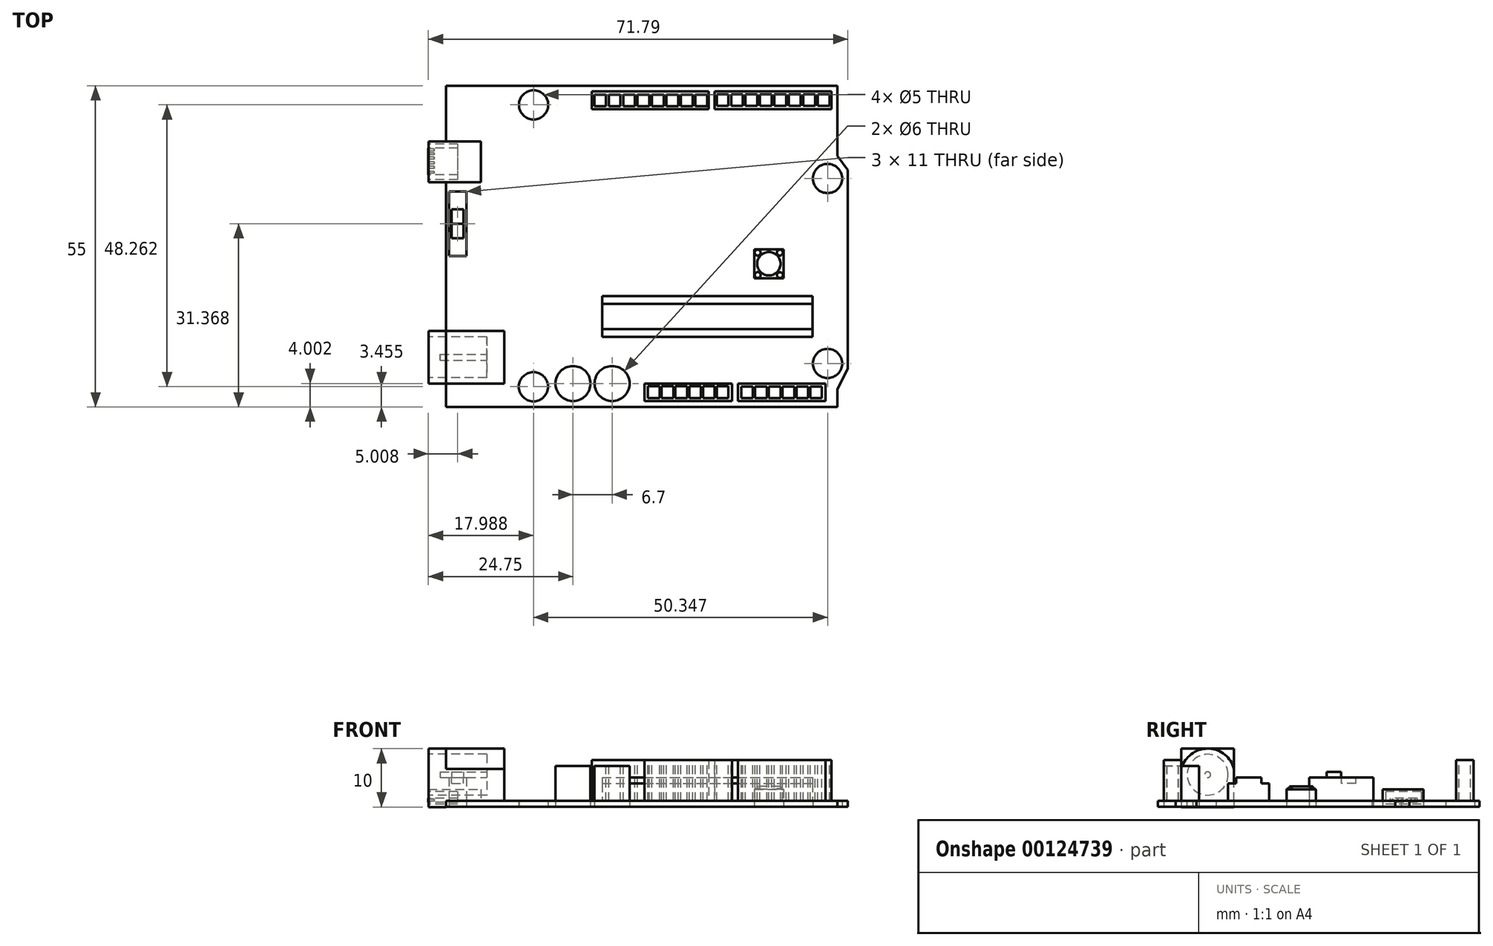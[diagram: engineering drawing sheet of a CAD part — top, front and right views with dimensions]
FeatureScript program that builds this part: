
annotation { "Feature Type Name" : "Feature", "Feature Type Description" : "" }
export const myFeature = defineFeature(function(context is Context, id is Id, definition is map)
    precondition{}
    {
        {
            var Q0;
            Q0=qCreatedBy(makeId("Top.planeOp"),FACE);
            var sketch = newSketch(context, id + "F0", { "sketchPlane" : qUnion([Q0])});
            skLineSegment(sketch, "E0.bottom", {"start": v(-37.2, 39.45) * mm, "end": v(29.8, 39.45) * mm});
            skLineSegment(sketch, "E0.top", {"start": v(-37.2, -15.55) * mm, "end": v(29.8, -15.55) * mm});
            skLineSegment(sketch, "E0.left", {"start": v(-37.2, 39.45) * mm, "end": v(-37.2, -15.55) * mm});
            skLineSegment(sketch, "E0.right", {"start": v(29.8, 39.45) * mm, "end": v(29.8, -15.55) * mm});
            skLineSegment(sketch, "E1", {"start": v(29.8, -12.55) * mm, "end": v(31.59, -8.97) * mm});
            skLineSegment(sketch, "E2", {"start": v(31.59, -8.97) * mm, "end": v(31.59, 25.03) * mm});
            skLineSegment(sketch, "E3", {"start": v(31.59, 25.03) * mm, "end": v(29.8, 27.45) * mm});
            skCircle(sketch, "E4", {"center": v(28.14, -8.11) * mm, "radius": 2.5 * mm});
            skCircle(sketch, "E5", {"center": v(-22.2, 36.17) * mm, "radius": 2.5 * mm});
            skCircle(sketch, "E6", {"center": v(28.14, 23.56) * mm, "radius": 2.5 * mm});
            skLineSegment(sketch, "E7", {"start": v(-22.2, 36.17) * mm, "end": v(-22.2, -14.2) * mm, "construction": true});
            skLineSegment(sketch, "E8", {"start": v(28.14, 23.56) * mm, "end": v(28.14, -13.38) * mm, "construction": true});
            skLineSegment(sketch, "E9.bottom", {"start": v(-40.2, 29.9) * mm, "end": v(-31.2, 29.9) * mm});
            skLineSegment(sketch, "E9.top", {"start": v(-40.2, 22.9) * mm, "end": v(-31.2, 22.9) * mm});
            skLineSegment(sketch, "E9.left", {"start": v(-40.2, 29.9) * mm, "end": v(-40.2, 22.9) * mm});
            skLineSegment(sketch, "E9.right", {"start": v(-31.2, 29.9) * mm, "end": v(-31.2, 22.9) * mm});
            skCircle(sketch, "E10", {"center": v(-22.21, -12.1) * mm, "radius": 2.5 * mm});
            skLineSegment(sketch, "E11.bottom", {"start": v(-3.2, -11.55) * mm, "end": v(11.8, -11.55) * mm});
            skLineSegment(sketch, "E11.top", {"start": v(-3.2, -14.55) * mm, "end": v(11.8, -14.55) * mm});
            skLineSegment(sketch, "E11.left", {"start": v(-3.2, -11.55) * mm, "end": v(-3.2, -14.55) * mm});
            skLineSegment(sketch, "E11.right", {"start": v(11.8, -11.55) * mm, "end": v(11.8, -14.55) * mm});
            skLineSegment(sketch, "E12.bottom", {"start": v(12.8, -11.55) * mm, "end": v(27.8, -11.55) * mm});
            skLineSegment(sketch, "E12.top", {"start": v(12.8, -14.55) * mm, "end": v(27.8, -14.55) * mm});
            skLineSegment(sketch, "E12.left", {"start": v(12.8, -11.55) * mm, "end": v(12.8, -14.55) * mm});
            skLineSegment(sketch, "E12.right", {"start": v(27.8, -11.55) * mm, "end": v(27.8, -14.55) * mm});
            skLineSegment(sketch, "E13.bottom", {"start": v(-12.2, 38.45) * mm, "end": v(7.8, 38.45) * mm});
            skLineSegment(sketch, "E13.top", {"start": v(-12.2, 35.45) * mm, "end": v(7.8, 35.45) * mm});
            skLineSegment(sketch, "E13.left", {"start": v(-12.2, 38.45) * mm, "end": v(-12.2, 35.45) * mm});
            skLineSegment(sketch, "E13.right", {"start": v(7.8, 38.45) * mm, "end": v(7.8, 35.45) * mm});
            skLineSegment(sketch, "E14.bottom", {"start": v(8.8, 38.45) * mm, "end": v(28.8, 38.45) * mm});
            skLineSegment(sketch, "E14.top", {"start": v(8.8, 35.45) * mm, "end": v(28.8, 35.45) * mm});
            skLineSegment(sketch, "E14.left", {"start": v(8.8, 38.45) * mm, "end": v(8.8, 35.45) * mm});
            skLineSegment(sketch, "E14.right", {"start": v(28.8, 38.45) * mm, "end": v(28.8, 35.45) * mm});
            skLineSegment(sketch, "E15.bottom", {"start": v(-10.41, 3.45) * mm, "end": v(25.59, 3.45) * mm});
            skLineSegment(sketch, "E15.top", {"start": v(-10.41, -3.55) * mm, "end": v(25.59, -3.55) * mm});
            skLineSegment(sketch, "E15.left", {"start": v(-10.41, 3.45) * mm, "end": v(-10.41, -3.55) * mm});
            skLineSegment(sketch, "E15.right", {"start": v(25.59, 3.45) * mm, "end": v(25.59, -3.55) * mm});
            skCircle(sketch, "E16", {"center": v(-8.75, -11.55) * mm, "radius": 3 * mm});
            skCircle(sketch, "E17", {"center": v(-15.45, -11.55) * mm, "radius": 3 * mm});
            skLineSegment(sketch, "E18", {"start": v(-3.2, -14.55) * mm, "end": v(-23.42, -14.6) * mm, "construction": true});
            skLineSegment(sketch, "E19.bottom", {"start": v(-36.7, 21.32) * mm, "end": v(-33.7, 21.32) * mm});
            skLineSegment(sketch, "E19.top", {"start": v(-36.7, 10.32) * mm, "end": v(-33.7, 10.32) * mm});
            skLineSegment(sketch, "E19.left", {"start": v(-36.7, 21.32) * mm, "end": v(-36.7, 10.32) * mm});
            skLineSegment(sketch, "E19.right", {"start": v(-33.7, 21.32) * mm, "end": v(-33.7, 10.32) * mm});
            skLineSegment(sketch, "E20.bottom", {"start": v(15.59, 11.45) * mm, "end": v(20.59, 11.45) * mm});
            skLineSegment(sketch, "E20.top", {"start": v(15.59, 6.45) * mm, "end": v(20.59, 6.45) * mm});
            skLineSegment(sketch, "E20.left", {"start": v(15.59, 11.45) * mm, "end": v(15.59, 6.45) * mm});
            skLineSegment(sketch, "E20.right", {"start": v(20.59, 11.45) * mm, "end": v(20.59, 6.45) * mm});
            skSolve(sketch);
        }
        {
            var Q0;
            {var subQ11=sQuery(id+"F0.wireOp",EDGE,"E0.bottom");Q0=makeQuery(id+"F0.imprint","IMPRINT",FACE,{"disambiguationData":[TD([[makeQuery(id+"F0.imprint","IMPRINT",EDGE,{"derivedFrom":subQ11}),-1.0]])]});}
            var Q1;
            {var subQ0=sQuery(id+"F0.wireOp",EDGE,"E1");Q1=makeQuery(id+"F0.imprint","IMPRINT",FACE,{"disambiguationData":[TD([[makeQuery(id+"F0.imprint","IMPRINT",EDGE,{"derivedFrom":subQ0}),1.0]])]});}
            extrude(context, id + "F1", {"entities" : qUnion([Q0, Q1]), "depth" : 1 * mm});
        }
        {
            var Q0;
            {var subQ5=sQuery(id+"F0.wireOp",EDGE,"E9.right");Q0=makeQuery(id+"F0.imprint","IMPRINT",FACE,{"disambiguationData":[TD([[makeQuery(id+"F0.imprint","IMPRINT",EDGE,{"derivedFrom":subQ5}),-1.0]])]});}
            var Q1;
            {var subQ5=sQuery(id+"F0.wireOp",EDGE,"E9.left");Q1=makeQuery(id+"F0.imprint","IMPRINT",FACE,{"disambiguationData":[TD([[makeQuery(id+"F0.imprint","IMPRINT",EDGE,{"derivedFrom":subQ5}),1.0]])]});}
            extrude(context, id + "F2", {"entities" : qUnion([Q0, Q1]), "operationType" : NewBodyOperationType.ADD, "depth" : 3 * mm});
        }
        {
            var Q0;
            Q0=makeQuery(id+"F2.opExtrude","SWEPT_FACE",FACE,{"disambiguationData":[OSD([sQuery(id+"F0.wireOp",EDGE,"E9.left")])]});
            var sketch = newSketch(context, id + "F3", { "sketchPlane" : qUnion([Q0])});
            skLineSegment(sketch, "E21.bottom", {"start": v(-29.48, 2.58) * mm, "end": v(-23.4, 2.58) * mm});
            skLineSegment(sketch, "E21.top", {"start": v(-29.48, 0.43) * mm, "end": v(-23.4, 0.43) * mm});
            skLineSegment(sketch, "E21.left", {"start": v(-29.48, 2.58) * mm, "end": v(-29.48, 0.43) * mm});
            skLineSegment(sketch, "E21.right", {"start": v(-23.4, 2.58) * mm, "end": v(-23.4, 0.43) * mm});
            skLineSegment(sketch, "E22.bottom", {"start": v(-28.8, 1.47) * mm, "end": v(-24.19, 1.47) * mm});
            skLineSegment(sketch, "E22.top", {"start": v(-28.8, 0.77) * mm, "end": v(-24.19, 0.77) * mm});
            skLineSegment(sketch, "E22.left", {"start": v(-28.8, 1.47) * mm, "end": v(-28.8, 0.77) * mm});
            skLineSegment(sketch, "E22.right", {"start": v(-24.19, 1.47) * mm, "end": v(-24.19, 0.77) * mm});
            skSolve(sketch);
        }
        {
            var Q0;
            Q0=makeQuery(id+"F3.imprint","IMPRINT",FACE,{"disambiguationData":[TD([[makeQuery(id+"F3.imprint","IMPRINT",EDGE,{"derivedFrom":sQuery(id+"F3.wireOp",EDGE,"E21.bottom")}),-1.0]])]});
            extrude(context, id + "F4", {"entities" : qUnion([Q0]), "operationType" : NewBodyOperationType.REMOVE, "oppositeDirection" : true, "depth" : 5 * mm});
        }
        {
            var Q0;
            Q0=makeQuery(id+"F4.boolean.opBoolean","SPLIT",FACE,{"disambiguationData":[TD([makeQuery(id+"F4.opExtrude","SWEPT_FACE",FACE,{"disambiguationData":[OSD([sQuery(id+"F3.wireOp",EDGE,"E22.bottom")])]})])],"derivedFrom":makeQuery(id+"F2.opExtrude","SWEPT_FACE",FACE,{"disambiguationData":[OSD([sQuery(id+"F0.wireOp",EDGE,"E9.left")])]})});
            extrude(context, id + "F5", {"entities" : qUnion([Q0]), "operationType" : NewBodyOperationType.ADD, "depth" : 0.01 * mm});
        }
        {
            var Q0;
            Q0=makeQuery(id+"F5.opExtrude","CAP_FACE",FACE,{"disambiguationData":[OSD([sQuery(id+"F0.wireOp",EDGE,"E9.left")])],"isStart":false});
            var sketch = newSketch(context, id + "F6", { "sketchPlane" : qUnion([Q0])});
            skCircle(sketch, "E23", {"center": v(-28.44, 1.13) * mm, "radius": 0.18 * mm});
            skCircle(sketch, "E24", {"center": v(-27.77, 1.13) * mm, "radius": 0.18 * mm});
            skCircle(sketch, "E25", {"center": v(-24.6, 1.13) * mm, "radius": 0.18 * mm});
            skCircle(sketch, "E26", {"center": v(-27.04, 1.14) * mm, "radius": 0.18 * mm});
            skCircle(sketch, "E27", {"center": v(-26.24, 1.13) * mm, "radius": 0.18 * mm});
            skCircle(sketch, "E28", {"center": v(-25.45, 1.13) * mm, "radius": 0.18 * mm});
            skSolve(sketch);
        }
        {
            var Q0;
            Q0=makeQuery(id+"F6.imprint","IMPRINT",FACE,{"disambiguationData":[TD([[makeQuery(id+"F6.imprint","IMPRINT",EDGE,{"derivedFrom":sQuery(id+"F6.wireOp",EDGE,"E23")}),1.0]])]});
            var Q1;
            Q1=makeQuery(id+"F6.imprint","IMPRINT",FACE,{"disambiguationData":[TD([[makeQuery(id+"F6.imprint","IMPRINT",EDGE,{"derivedFrom":sQuery(id+"F6.wireOp",EDGE,"E24")}),1.0]])]});
            var Q2;
            Q2=makeQuery(id+"F6.imprint","IMPRINT",FACE,{"disambiguationData":[TD([[makeQuery(id+"F6.imprint","IMPRINT",EDGE,{"derivedFrom":sQuery(id+"F6.wireOp",EDGE,"E26")}),1.0]])]});
            var Q3;
            Q3=makeQuery(id+"F6.imprint","IMPRINT",FACE,{"disambiguationData":[TD([[makeQuery(id+"F6.imprint","IMPRINT",EDGE,{"derivedFrom":sQuery(id+"F6.wireOp",EDGE,"E27")}),1.0]])]});
            var Q4;
            Q4=makeQuery(id+"F6.imprint","IMPRINT",FACE,{"disambiguationData":[TD([[makeQuery(id+"F6.imprint","IMPRINT",EDGE,{"derivedFrom":sQuery(id+"F6.wireOp",EDGE,"E28")}),1.0]])]});
            var Q5;
            Q5=makeQuery(id+"F6.imprint","IMPRINT",FACE,{"disambiguationData":[TD([[makeQuery(id+"F6.imprint","IMPRINT",EDGE,{"derivedFrom":sQuery(id+"F6.wireOp",EDGE,"E25")}),1.0]])]});
            var Q6;
            Q6=sQuery(id+"F6.wireOp",EDGE,"E23");
            var Q7;
            Q7=sQuery(id+"F6.wireOp",EDGE,"E24");
            var Q8;
            Q8=sQuery(id+"F6.wireOp",EDGE,"E26");
            var Q9;
            Q9=sQuery(id+"F6.wireOp",EDGE,"E27");
            var Q10;
            Q10=sQuery(id+"F6.wireOp",EDGE,"E28");
            var Q11;
            Q11=sQuery(id+"F6.wireOp",EDGE,"E25");
            extrude(context, id + "F7", {"entities" : qUnion([Q0, Q1, Q2, Q3, Q4, Q5]), "operationType" : NewBodyOperationType.REMOVE, "surfaceEntities" : qUnion([Q6, Q7, Q8, Q9, Q10, Q11]), "oppositeDirection" : true, "depth" : 1 * mm});
        }
        {
            var Q0;
            Q0=makeQuery(id+"F0.imprint","IMPRINT",FACE,{"disambiguationData":[TD([[makeQuery(id+"F0.imprint","IMPRINT",EDGE,{"derivedFrom":sQuery(id+"F0.wireOp",EDGE,"E11.bottom")}),-1.0]])]});
            var Q1;
            Q1=makeQuery(id+"F0.imprint","IMPRINT",FACE,{"disambiguationData":[TD([[makeQuery(id+"F0.imprint","IMPRINT",EDGE,{"derivedFrom":sQuery(id+"F0.wireOp",EDGE,"E12.bottom")}),-1.0]])]});
            extrude(context, id + "F8", {"entities" : qUnion([Q0, Q1]), "operationType" : NewBodyOperationType.ADD, "depth" : 8 * mm});
        }
        {
            var Q0;
            Q0=makeQuery(id+"F8.opExtrude","CAP_FACE",FACE,{"disambiguationData":[OSD([sQuery(id+"F0.wireOp",EDGE,"E11.bottom"),sQuery(id+"F0.wireOp",EDGE,"E11.top"),sQuery(id+"F0.wireOp",EDGE,"E11.left"),sQuery(id+"F0.wireOp",EDGE,"E11.right")])],"isStart":false});
            var sketch = newSketch(context, id + "F9", { "sketchPlane" : qUnion([Q0])});
            skLineSegment(sketch, "E29.bottom", {"start": v(-2.63, -12.01) * mm, "end": v(-0.63, -12.01) * mm});
            skLineSegment(sketch, "E29.top", {"start": v(-2.63, -14.01) * mm, "end": v(-0.63, -14.01) * mm});
            skLineSegment(sketch, "E29.left", {"start": v(-2.63, -12.01) * mm, "end": v(-2.63, -14.01) * mm});
            skLineSegment(sketch, "E29.right", {"start": v(-0.63, -12.01) * mm, "end": v(-0.63, -14.01) * mm});
            skLineSegment(sketch, "E30.1.0.0", {"start": v(-0.27, -12.01) * mm, "end": v(1.73, -12.01) * mm});
            skLineSegment(sketch, "E30.1.0.1", {"start": v(1.73, -12.01) * mm, "end": v(1.73, -14.01) * mm});
            skLineSegment(sketch, "E30.1.0.2", {"start": v(-0.27, -12.01) * mm, "end": v(-0.27, -14.01) * mm});
            skLineSegment(sketch, "E30.1.0.3", {"start": v(-0.27, -14.01) * mm, "end": v(1.73, -14.01) * mm});
            skLineSegment(sketch, "E30.2.0.0", {"start": v(2.1, -12.01) * mm, "end": v(4.1, -12.01) * mm});
            skLineSegment(sketch, "E30.2.0.1", {"start": v(4.1, -12.01) * mm, "end": v(4.1, -14.01) * mm});
            skLineSegment(sketch, "E30.2.0.2", {"start": v(2.1, -12.01) * mm, "end": v(2.1, -14.01) * mm});
            skLineSegment(sketch, "E30.2.0.3", {"start": v(2.1, -14.01) * mm, "end": v(4.1, -14.01) * mm});
            skLineSegment(sketch, "E30.3.0.0", {"start": v(4.45, -12.01) * mm, "end": v(6.45, -12.01) * mm});
            skLineSegment(sketch, "E30.3.0.1", {"start": v(6.45, -12.01) * mm, "end": v(6.45, -14.01) * mm});
            skLineSegment(sketch, "E30.3.0.2", {"start": v(4.45, -12.01) * mm, "end": v(4.45, -14.01) * mm});
            skLineSegment(sketch, "E30.3.0.3", {"start": v(4.45, -14.01) * mm, "end": v(6.45, -14.01) * mm});
            skLineSegment(sketch, "E30.4.0.0", {"start": v(6.8, -12.01) * mm, "end": v(8.8, -12.01) * mm});
            skLineSegment(sketch, "E30.4.0.1", {"start": v(8.8, -12.01) * mm, "end": v(8.8, -14.01) * mm});
            skLineSegment(sketch, "E30.4.0.2", {"start": v(6.8, -12.01) * mm, "end": v(6.8, -14.01) * mm});
            skLineSegment(sketch, "E30.4.0.3", {"start": v(6.8, -14.01) * mm, "end": v(8.8, -14.01) * mm});
            skLineSegment(sketch, "E30.5.0.0", {"start": v(9.17, -12.01) * mm, "end": v(11.17, -12.01) * mm});
            skLineSegment(sketch, "E30.5.0.1", {"start": v(11.17, -12.01) * mm, "end": v(11.17, -14.01) * mm});
            skLineSegment(sketch, "E30.5.0.2", {"start": v(9.17, -12.01) * mm, "end": v(9.17, -14.01) * mm});
            skLineSegment(sketch, "E30.5.0.3", {"start": v(9.17, -14.01) * mm, "end": v(11.17, -14.01) * mm});
            skLineSegment(sketch, "E30.direction1", {"start": v(-2.63, -12.01) * mm, "end": v(-0.27, -12.01) * mm, "construction": true});
            skLineSegment(sketch, "E31.bottom", {"start": v(13.37, -12.06) * mm, "end": v(15.37, -12.06) * mm});
            skLineSegment(sketch, "E31.top", {"start": v(13.37, -14.06) * mm, "end": v(15.37, -14.06) * mm});
            skLineSegment(sketch, "E31.left", {"start": v(13.37, -12.06) * mm, "end": v(13.37, -14.06) * mm});
            skLineSegment(sketch, "E31.right", {"start": v(15.37, -12.06) * mm, "end": v(15.37, -14.06) * mm});
            skLineSegment(sketch, "E32.1.0.0", {"start": v(15.73, -12.06) * mm, "end": v(17.73, -12.06) * mm});
            skLineSegment(sketch, "E32.1.0.1", {"start": v(17.73, -12.06) * mm, "end": v(17.73, -14.06) * mm});
            skLineSegment(sketch, "E32.1.0.2", {"start": v(15.73, -12.06) * mm, "end": v(15.73, -14.06) * mm});
            skLineSegment(sketch, "E32.1.0.3", {"start": v(15.73, -14.06) * mm, "end": v(17.73, -14.06) * mm});
            skLineSegment(sketch, "E32.2.0.0", {"start": v(18.09, -12.06) * mm, "end": v(20.09, -12.06) * mm});
            skLineSegment(sketch, "E32.2.0.1", {"start": v(20.09, -12.06) * mm, "end": v(20.09, -14.06) * mm});
            skLineSegment(sketch, "E32.2.0.2", {"start": v(18.09, -12.06) * mm, "end": v(18.09, -14.06) * mm});
            skLineSegment(sketch, "E32.2.0.3", {"start": v(18.09, -14.06) * mm, "end": v(20.09, -14.06) * mm});
            skLineSegment(sketch, "E32.3.0.0", {"start": v(20.45, -12.06) * mm, "end": v(22.45, -12.06) * mm});
            skLineSegment(sketch, "E32.3.0.1", {"start": v(22.45, -12.06) * mm, "end": v(22.45, -14.06) * mm});
            skLineSegment(sketch, "E32.3.0.2", {"start": v(20.45, -12.06) * mm, "end": v(20.45, -14.06) * mm});
            skLineSegment(sketch, "E32.3.0.3", {"start": v(20.45, -14.06) * mm, "end": v(22.45, -14.06) * mm});
            skLineSegment(sketch, "E32.4.0.0", {"start": v(22.8, -12.06) * mm, "end": v(24.8, -12.06) * mm});
            skLineSegment(sketch, "E32.4.0.1", {"start": v(24.8, -12.06) * mm, "end": v(24.8, -14.06) * mm});
            skLineSegment(sketch, "E32.4.0.2", {"start": v(22.8, -12.06) * mm, "end": v(22.8, -14.06) * mm});
            skLineSegment(sketch, "E32.4.0.3", {"start": v(22.8, -14.06) * mm, "end": v(24.8, -14.06) * mm});
            skLineSegment(sketch, "E32.5.0.0", {"start": v(25.16, -12.06) * mm, "end": v(27.16, -12.06) * mm});
            skLineSegment(sketch, "E32.5.0.1", {"start": v(27.16, -12.06) * mm, "end": v(27.16, -14.06) * mm});
            skLineSegment(sketch, "E32.5.0.2", {"start": v(25.16, -12.06) * mm, "end": v(25.16, -14.06) * mm});
            skLineSegment(sketch, "E32.5.0.3", {"start": v(25.16, -14.06) * mm, "end": v(27.16, -14.06) * mm});
            skLineSegment(sketch, "E32.direction1", {"start": v(13.37, -12.06) * mm, "end": v(15.73, -12.06) * mm, "construction": true});
            skSolve(sketch);
        }
        {
            var Q0;
            Q0=makeQuery(id+"F9.imprint","IMPRINT",FACE,{"disambiguationData":[TD([[makeQuery(id+"F9.imprint","IMPRINT",EDGE,{"derivedFrom":sQuery(id+"F9.wireOp",EDGE,"E29.bottom")}),-1.0]])]});
            var Q1;
            Q1=makeQuery(id+"F9.imprint","IMPRINT",FACE,{"disambiguationData":[TD([[makeQuery(id+"F9.imprint","IMPRINT",EDGE,{"derivedFrom":sQuery(id+"F9.wireOp",EDGE,"E30.1.0.0")}),-1.0]])]});
            var Q2;
            Q2=makeQuery(id+"F9.imprint","IMPRINT",FACE,{"disambiguationData":[TD([[makeQuery(id+"F9.imprint","IMPRINT",EDGE,{"derivedFrom":sQuery(id+"F9.wireOp",EDGE,"E30.2.0.0")}),-1.0]])]});
            var Q3;
            Q3=makeQuery(id+"F9.imprint","IMPRINT",FACE,{"disambiguationData":[TD([[makeQuery(id+"F9.imprint","IMPRINT",EDGE,{"derivedFrom":sQuery(id+"F9.wireOp",EDGE,"E30.3.0.0")}),-1.0]])]});
            var Q4;
            Q4=makeQuery(id+"F9.imprint","IMPRINT",FACE,{"disambiguationData":[TD([[makeQuery(id+"F9.imprint","IMPRINT",EDGE,{"derivedFrom":sQuery(id+"F9.wireOp",EDGE,"E30.4.0.0")}),-1.0]])]});
            var Q5;
            Q5=makeQuery(id+"F9.imprint","IMPRINT",FACE,{"disambiguationData":[TD([[makeQuery(id+"F9.imprint","IMPRINT",EDGE,{"derivedFrom":sQuery(id+"F9.wireOp",EDGE,"E30.5.0.0")}),-1.0]])]});
            var Q6;
            Q6=makeQuery(id+"F9.imprint","IMPRINT",FACE,{"disambiguationData":[TD([[makeQuery(id+"F9.imprint","IMPRINT",EDGE,{"derivedFrom":sQuery(id+"F9.wireOp",EDGE,"E31.bottom")}),-1.0]])]});
            var Q7;
            Q7=makeQuery(id+"F9.imprint","IMPRINT",FACE,{"disambiguationData":[TD([[makeQuery(id+"F9.imprint","IMPRINT",EDGE,{"derivedFrom":sQuery(id+"F9.wireOp",EDGE,"E32.1.0.0")}),-1.0]])]});
            var Q8;
            Q8=makeQuery(id+"F9.imprint","IMPRINT",FACE,{"disambiguationData":[TD([[makeQuery(id+"F9.imprint","IMPRINT",EDGE,{"derivedFrom":sQuery(id+"F9.wireOp",EDGE,"E32.2.0.0")}),-1.0]])]});
            var Q9;
            Q9=makeQuery(id+"F9.imprint","IMPRINT",FACE,{"disambiguationData":[TD([[makeQuery(id+"F9.imprint","IMPRINT",EDGE,{"derivedFrom":sQuery(id+"F9.wireOp",EDGE,"E32.3.0.0")}),-1.0]])]});
            var Q10;
            Q10=makeQuery(id+"F9.imprint","IMPRINT",FACE,{"disambiguationData":[TD([[makeQuery(id+"F9.imprint","IMPRINT",EDGE,{"derivedFrom":sQuery(id+"F9.wireOp",EDGE,"E32.4.0.0")}),-1.0]])]});
            var Q11;
            Q11=makeQuery(id+"F9.imprint","IMPRINT",FACE,{"disambiguationData":[TD([[makeQuery(id+"F9.imprint","IMPRINT",EDGE,{"derivedFrom":sQuery(id+"F9.wireOp",EDGE,"E32.5.0.0")}),-1.0]])]});
            var Q12;
            Q12=sQuery(id+"F9.wireOp",EDGE,"e2aa6071-b982-4bc8-af80-e95c8fd193ff.bottom");
            var Q13;
            Q13=sQuery(id+"F9.wireOp",EDGE,"e2aa6071-b982-4bc8-af80-e95c8fd193ff.top");
            var Q14;
            Q14=sQuery(id+"F9.wireOp",EDGE,"e2aa6071-b982-4bc8-af80-e95c8fd193ff.left");
            var Q15;
            Q15=sQuery(id+"F9.wireOp",EDGE,"e2aa6071-b982-4bc8-af80-e95c8fd193ff.right");
            var Q16;
            Q16=sQuery(id+"F9.wireOp",EDGE,"8d807763-f77d-4302-8a10-7eaa0a08b874.1.0.0");
            var Q17;
            Q17=sQuery(id+"F9.wireOp",EDGE,"8d807763-f77d-4302-8a10-7eaa0a08b874.1.0.1");
            var Q18;
            Q18=sQuery(id+"F9.wireOp",EDGE,"8d807763-f77d-4302-8a10-7eaa0a08b874.1.0.2");
            var Q19;
            Q19=sQuery(id+"F9.wireOp",EDGE,"8d807763-f77d-4302-8a10-7eaa0a08b874.1.0.3");
            var Q20;
            Q20=sQuery(id+"F9.wireOp",EDGE,"8d807763-f77d-4302-8a10-7eaa0a08b874.2.0.0");
            var Q21;
            Q21=sQuery(id+"F9.wireOp",EDGE,"8d807763-f77d-4302-8a10-7eaa0a08b874.2.0.1");
            var Q22;
            Q22=sQuery(id+"F9.wireOp",EDGE,"8d807763-f77d-4302-8a10-7eaa0a08b874.2.0.2");
            var Q23;
            Q23=sQuery(id+"F9.wireOp",EDGE,"8d807763-f77d-4302-8a10-7eaa0a08b874.2.0.3");
            var Q24;
            Q24=sQuery(id+"F9.wireOp",EDGE,"8d807763-f77d-4302-8a10-7eaa0a08b874.3.0.0");
            var Q25;
            Q25=sQuery(id+"F9.wireOp",EDGE,"8d807763-f77d-4302-8a10-7eaa0a08b874.3.0.1");
            var Q26;
            Q26=sQuery(id+"F9.wireOp",EDGE,"8d807763-f77d-4302-8a10-7eaa0a08b874.3.0.2");
            var Q27;
            Q27=sQuery(id+"F9.wireOp",EDGE,"8d807763-f77d-4302-8a10-7eaa0a08b874.3.0.3");
            var Q28;
            Q28=sQuery(id+"F9.wireOp",EDGE,"8d807763-f77d-4302-8a10-7eaa0a08b874.4.0.0");
            var Q29;
            Q29=sQuery(id+"F9.wireOp",EDGE,"8d807763-f77d-4302-8a10-7eaa0a08b874.4.0.1");
            var Q30;
            Q30=sQuery(id+"F9.wireOp",EDGE,"8d807763-f77d-4302-8a10-7eaa0a08b874.4.0.2");
            var Q31;
            Q31=sQuery(id+"F9.wireOp",EDGE,"8d807763-f77d-4302-8a10-7eaa0a08b874.4.0.3");
            var Q32;
            Q32=sQuery(id+"F9.wireOp",EDGE,"8d807763-f77d-4302-8a10-7eaa0a08b874.5.0.0");
            var Q33;
            Q33=sQuery(id+"F9.wireOp",EDGE,"8d807763-f77d-4302-8a10-7eaa0a08b874.5.0.1");
            var Q34;
            Q34=sQuery(id+"F9.wireOp",EDGE,"8d807763-f77d-4302-8a10-7eaa0a08b874.5.0.2");
            var Q35;
            Q35=sQuery(id+"F9.wireOp",EDGE,"8d807763-f77d-4302-8a10-7eaa0a08b874.5.0.3");
            extrude(context, id + "F10", {"entities" : qUnion([Q0, Q1, Q2, Q3, Q4, Q5, Q6, Q7, Q8, Q9, Q10, Q11]), "operationType" : NewBodyOperationType.REMOVE, "surfaceEntities" : qUnion([Q12, Q13, Q14, Q15, Q16, Q17, Q18, Q19, Q20, Q21, Q22, Q23, Q24, Q25, Q26, Q27, Q28, Q29, Q30, Q31, Q32, Q33, Q34, Q35]), "oppositeDirection" : true, "depth" : 7 * mm});
        }
        {
            var Q0;
            Q0=makeQuery(id+"F0.imprint","IMPRINT",FACE,{"disambiguationData":[TD([[makeQuery(id+"F0.imprint","IMPRINT",EDGE,{"derivedFrom":sQuery(id+"F0.wireOp",EDGE,"E13.bottom")}),-1.0]])]});
            var Q1;
            Q1=makeQuery(id+"F0.imprint","IMPRINT",FACE,{"disambiguationData":[TD([[makeQuery(id+"F0.imprint","IMPRINT",EDGE,{"derivedFrom":sQuery(id+"F0.wireOp",EDGE,"E14.bottom")}),-1.0]])]});
            extrude(context, id + "F11", {"entities" : qUnion([Q0, Q1]), "operationType" : NewBodyOperationType.ADD, "depth" : 8 * mm});
        }
        {
            var Q0;
            Q0=makeQuery(id+"F11.opExtrude","CAP_FACE",FACE,{"disambiguationData":[OSD([sQuery(id+"F0.wireOp",EDGE,"E13.bottom"),sQuery(id+"F0.wireOp",EDGE,"E13.top"),sQuery(id+"F0.wireOp",EDGE,"E13.left"),sQuery(id+"F0.wireOp",EDGE,"E13.right")])],"isStart":false});
            var sketch = newSketch(context, id + "F12", { "sketchPlane" : qUnion([Q0])});
            skLineSegment(sketch, "E33.bottom", {"start": v(-11.8, 37.93) * mm, "end": v(-9.8, 37.93) * mm});
            skLineSegment(sketch, "E33.top", {"start": v(-11.8, 35.93) * mm, "end": v(-9.8, 35.93) * mm});
            skLineSegment(sketch, "E33.left", {"start": v(-11.8, 37.93) * mm, "end": v(-11.8, 35.93) * mm});
            skLineSegment(sketch, "E33.right", {"start": v(-9.8, 37.93) * mm, "end": v(-9.8, 35.93) * mm});
            skLineSegment(sketch, "E34.1.0.0", {"start": v(-9.32, 35.93) * mm, "end": v(-7.32, 35.93) * mm});
            skLineSegment(sketch, "E34.1.0.1", {"start": v(-9.32, 37.93) * mm, "end": v(-9.32, 35.93) * mm});
            skLineSegment(sketch, "E34.1.0.2", {"start": v(-7.32, 37.93) * mm, "end": v(-7.32, 35.93) * mm});
            skLineSegment(sketch, "E34.1.0.3", {"start": v(-9.32, 37.93) * mm, "end": v(-7.32, 37.93) * mm});
            skLineSegment(sketch, "E34.2.0.0", {"start": v(-6.85, 35.93) * mm, "end": v(-4.85, 35.93) * mm});
            skLineSegment(sketch, "E34.2.0.1", {"start": v(-6.85, 37.93) * mm, "end": v(-6.85, 35.93) * mm});
            skLineSegment(sketch, "E34.2.0.2", {"start": v(-4.85, 37.93) * mm, "end": v(-4.85, 35.93) * mm});
            skLineSegment(sketch, "E34.2.0.3", {"start": v(-6.85, 37.93) * mm, "end": v(-4.85, 37.93) * mm});
            skLineSegment(sketch, "E34.3.0.0", {"start": v(-4.38, 35.93) * mm, "end": v(-2.38, 35.93) * mm});
            skLineSegment(sketch, "E34.3.0.1", {"start": v(-4.38, 37.93) * mm, "end": v(-4.38, 35.93) * mm});
            skLineSegment(sketch, "E34.3.0.2", {"start": v(-2.38, 37.93) * mm, "end": v(-2.38, 35.93) * mm});
            skLineSegment(sketch, "E34.3.0.3", {"start": v(-4.38, 37.93) * mm, "end": v(-2.38, 37.93) * mm});
            skLineSegment(sketch, "E34.4.0.0", {"start": v(-1.9, 35.93) * mm, "end": v(0.1, 35.93) * mm});
            skLineSegment(sketch, "E34.4.0.1", {"start": v(-1.9, 37.93) * mm, "end": v(-1.9, 35.93) * mm});
            skLineSegment(sketch, "E34.4.0.2", {"start": v(0.1, 37.93) * mm, "end": v(0.1, 35.93) * mm});
            skLineSegment(sketch, "E34.4.0.3", {"start": v(-1.9, 37.93) * mm, "end": v(0.1, 37.93) * mm});
            skLineSegment(sketch, "E34.5.0.0", {"start": v(0.57, 35.93) * mm, "end": v(2.57, 35.93) * mm});
            skLineSegment(sketch, "E34.5.0.1", {"start": v(0.57, 37.93) * mm, "end": v(0.57, 35.93) * mm});
            skLineSegment(sketch, "E34.5.0.2", {"start": v(2.57, 37.93) * mm, "end": v(2.57, 35.93) * mm});
            skLineSegment(sketch, "E34.5.0.3", {"start": v(0.57, 37.93) * mm, "end": v(2.57, 37.93) * mm});
            skLineSegment(sketch, "E34.6.0.0", {"start": v(3.04, 35.93) * mm, "end": v(5.04, 35.93) * mm});
            skLineSegment(sketch, "E34.6.0.1", {"start": v(3.04, 37.93) * mm, "end": v(3.04, 35.93) * mm});
            skLineSegment(sketch, "E34.6.0.2", {"start": v(5.04, 37.93) * mm, "end": v(5.04, 35.93) * mm});
            skLineSegment(sketch, "E34.6.0.3", {"start": v(3.04, 37.93) * mm, "end": v(5.04, 37.93) * mm});
            skLineSegment(sketch, "E34.7.0.0", {"start": v(5.5, 35.93) * mm, "end": v(7.5, 35.93) * mm});
            skLineSegment(sketch, "E34.7.0.1", {"start": v(5.5, 37.93) * mm, "end": v(5.5, 35.93) * mm});
            skLineSegment(sketch, "E34.7.0.2", {"start": v(7.5, 37.93) * mm, "end": v(7.5, 35.93) * mm});
            skLineSegment(sketch, "E34.7.0.3", {"start": v(5.5, 37.93) * mm, "end": v(7.5, 37.93) * mm});
            skLineSegment(sketch, "E34.direction1", {"start": v(-11.8, 35.93) * mm, "end": v(-9.32, 35.93) * mm, "construction": true});
            skLineSegment(sketch, "E35.bottom", {"start": v(9.16, 37.98) * mm, "end": v(11.16, 37.98) * mm});
            skLineSegment(sketch, "E35.top", {"start": v(9.16, 35.98) * mm, "end": v(11.16, 35.98) * mm});
            skLineSegment(sketch, "E35.left", {"start": v(9.16, 37.98) * mm, "end": v(9.16, 35.98) * mm});
            skLineSegment(sketch, "E35.right", {"start": v(11.16, 37.98) * mm, "end": v(11.16, 35.98) * mm});
            skLineSegment(sketch, "E36.1.0.0", {"start": v(11.63, 35.98) * mm, "end": v(13.63, 35.98) * mm});
            skLineSegment(sketch, "E36.1.0.1", {"start": v(11.63, 37.98) * mm, "end": v(11.63, 35.98) * mm});
            skLineSegment(sketch, "E36.1.0.2", {"start": v(13.63, 37.98) * mm, "end": v(13.63, 35.98) * mm});
            skLineSegment(sketch, "E36.1.0.3", {"start": v(11.63, 37.98) * mm, "end": v(13.63, 37.98) * mm});
            skLineSegment(sketch, "E36.2.0.0", {"start": v(14.1, 35.98) * mm, "end": v(16.1, 35.98) * mm});
            skLineSegment(sketch, "E36.2.0.1", {"start": v(14.1, 37.98) * mm, "end": v(14.1, 35.98) * mm});
            skLineSegment(sketch, "E36.2.0.2", {"start": v(16.1, 37.98) * mm, "end": v(16.1, 35.98) * mm});
            skLineSegment(sketch, "E36.2.0.3", {"start": v(14.1, 37.98) * mm, "end": v(16.1, 37.98) * mm});
            skLineSegment(sketch, "E36.3.0.0", {"start": v(16.57, 35.98) * mm, "end": v(18.57, 35.98) * mm});
            skLineSegment(sketch, "E36.3.0.1", {"start": v(16.57, 37.98) * mm, "end": v(16.57, 35.98) * mm});
            skLineSegment(sketch, "E36.3.0.2", {"start": v(18.57, 37.98) * mm, "end": v(18.57, 35.98) * mm});
            skLineSegment(sketch, "E36.3.0.3", {"start": v(16.57, 37.98) * mm, "end": v(18.57, 37.98) * mm});
            skLineSegment(sketch, "E36.4.0.0", {"start": v(19.04, 35.98) * mm, "end": v(21.04, 35.98) * mm});
            skLineSegment(sketch, "E36.4.0.1", {"start": v(19.04, 37.98) * mm, "end": v(19.04, 35.98) * mm});
            skLineSegment(sketch, "E36.4.0.2", {"start": v(21.04, 37.98) * mm, "end": v(21.04, 35.98) * mm});
            skLineSegment(sketch, "E36.4.0.3", {"start": v(19.04, 37.98) * mm, "end": v(21.04, 37.98) * mm});
            skLineSegment(sketch, "E36.5.0.0", {"start": v(21.51, 35.98) * mm, "end": v(23.51, 35.98) * mm});
            skLineSegment(sketch, "E36.5.0.1", {"start": v(21.51, 37.98) * mm, "end": v(21.51, 35.98) * mm});
            skLineSegment(sketch, "E36.5.0.2", {"start": v(23.51, 37.98) * mm, "end": v(23.51, 35.98) * mm});
            skLineSegment(sketch, "E36.5.0.3", {"start": v(21.51, 37.98) * mm, "end": v(23.51, 37.98) * mm});
            skLineSegment(sketch, "E36.6.0.0", {"start": v(23.99, 35.98) * mm, "end": v(25.99, 35.98) * mm});
            skLineSegment(sketch, "E36.6.0.1", {"start": v(23.99, 37.98) * mm, "end": v(23.99, 35.98) * mm});
            skLineSegment(sketch, "E36.6.0.2", {"start": v(25.99, 37.98) * mm, "end": v(25.99, 35.98) * mm});
            skLineSegment(sketch, "E36.6.0.3", {"start": v(23.99, 37.98) * mm, "end": v(25.99, 37.98) * mm});
            skLineSegment(sketch, "E36.7.0.0", {"start": v(26.46, 35.98) * mm, "end": v(28.46, 35.98) * mm});
            skLineSegment(sketch, "E36.7.0.1", {"start": v(26.46, 37.98) * mm, "end": v(26.46, 35.98) * mm});
            skLineSegment(sketch, "E36.7.0.2", {"start": v(28.46, 37.98) * mm, "end": v(28.46, 35.98) * mm});
            skLineSegment(sketch, "E36.7.0.3", {"start": v(26.46, 37.98) * mm, "end": v(28.46, 37.98) * mm});
            skLineSegment(sketch, "E36.direction1", {"start": v(9.16, 35.98) * mm, "end": v(11.63, 35.98) * mm, "construction": true});
            skSolve(sketch);
        }
        {
            var Q0;
            Q0=makeQuery(id+"F12.imprint","IMPRINT",FACE,{"disambiguationData":[TD([[makeQuery(id+"F12.imprint","IMPRINT",EDGE,{"derivedFrom":sQuery(id+"F12.wireOp",EDGE,"E33.bottom")}),-1.0]])]});
            var Q1;
            Q1=makeQuery(id+"F12.imprint","IMPRINT",FACE,{"disambiguationData":[TD([[makeQuery(id+"F12.imprint","IMPRINT",EDGE,{"derivedFrom":sQuery(id+"F12.wireOp",EDGE,"E34.1.0.0")}),1.0]])]});
            var Q2;
            Q2=makeQuery(id+"F12.imprint","IMPRINT",FACE,{"disambiguationData":[TD([[makeQuery(id+"F12.imprint","IMPRINT",EDGE,{"derivedFrom":sQuery(id+"F12.wireOp",EDGE,"E34.2.0.0")}),1.0]])]});
            var Q3;
            Q3=makeQuery(id+"F12.imprint","IMPRINT",FACE,{"disambiguationData":[TD([[makeQuery(id+"F12.imprint","IMPRINT",EDGE,{"derivedFrom":sQuery(id+"F12.wireOp",EDGE,"E34.3.0.0")}),1.0]])]});
            var Q4;
            Q4=makeQuery(id+"F12.imprint","IMPRINT",FACE,{"disambiguationData":[TD([[makeQuery(id+"F12.imprint","IMPRINT",EDGE,{"derivedFrom":sQuery(id+"F12.wireOp",EDGE,"E34.7.0.0")}),1.0]])]});
            var Q5;
            Q5=makeQuery(id+"F12.imprint","IMPRINT",FACE,{"disambiguationData":[TD([[makeQuery(id+"F12.imprint","IMPRINT",EDGE,{"derivedFrom":sQuery(id+"F12.wireOp",EDGE,"E34.6.0.0")}),1.0]])]});
            var Q6;
            Q6=makeQuery(id+"F12.imprint","IMPRINT",FACE,{"disambiguationData":[TD([[makeQuery(id+"F12.imprint","IMPRINT",EDGE,{"derivedFrom":sQuery(id+"F12.wireOp",EDGE,"E34.5.0.0")}),1.0]])]});
            var Q7;
            Q7=makeQuery(id+"F12.imprint","IMPRINT",FACE,{"disambiguationData":[TD([[makeQuery(id+"F12.imprint","IMPRINT",EDGE,{"derivedFrom":sQuery(id+"F12.wireOp",EDGE,"E34.4.0.0")}),1.0]])]});
            var Q8;
            Q8=makeQuery(id+"F12.imprint","IMPRINT",FACE,{"disambiguationData":[TD([[makeQuery(id+"F12.imprint","IMPRINT",EDGE,{"derivedFrom":sQuery(id+"F12.wireOp",EDGE,"E35.bottom")}),-1.0]])]});
            var Q9;
            Q9=makeQuery(id+"F12.imprint","IMPRINT",FACE,{"disambiguationData":[TD([[makeQuery(id+"F12.imprint","IMPRINT",EDGE,{"derivedFrom":sQuery(id+"F12.wireOp",EDGE,"E36.1.0.0")}),1.0]])]});
            var Q10;
            Q10=makeQuery(id+"F12.imprint","IMPRINT",FACE,{"disambiguationData":[TD([[makeQuery(id+"F12.imprint","IMPRINT",EDGE,{"derivedFrom":sQuery(id+"F12.wireOp",EDGE,"E36.2.0.0")}),1.0]])]});
            var Q11;
            Q11=makeQuery(id+"F12.imprint","IMPRINT",FACE,{"disambiguationData":[TD([[makeQuery(id+"F12.imprint","IMPRINT",EDGE,{"derivedFrom":sQuery(id+"F12.wireOp",EDGE,"E36.3.0.0")}),1.0]])]});
            var Q12;
            Q12=makeQuery(id+"F12.imprint","IMPRINT",FACE,{"disambiguationData":[TD([[makeQuery(id+"F12.imprint","IMPRINT",EDGE,{"derivedFrom":sQuery(id+"F12.wireOp",EDGE,"E36.4.0.0")}),1.0]])]});
            var Q13;
            Q13=makeQuery(id+"F12.imprint","IMPRINT",FACE,{"disambiguationData":[TD([[makeQuery(id+"F12.imprint","IMPRINT",EDGE,{"derivedFrom":sQuery(id+"F12.wireOp",EDGE,"E36.5.0.0")}),1.0]])]});
            var Q14;
            Q14=makeQuery(id+"F12.imprint","IMPRINT",FACE,{"disambiguationData":[TD([[makeQuery(id+"F12.imprint","IMPRINT",EDGE,{"derivedFrom":sQuery(id+"F12.wireOp",EDGE,"E36.6.0.0")}),1.0]])]});
            var Q15;
            Q15=makeQuery(id+"F12.imprint","IMPRINT",FACE,{"disambiguationData":[TD([[makeQuery(id+"F12.imprint","IMPRINT",EDGE,{"derivedFrom":sQuery(id+"F12.wireOp",EDGE,"E36.7.0.0")}),1.0]])]});
            var Q16;
            Q16=sQuery(id+"F12.wireOp",EDGE,"E35.bottom");
            var Q17;
            Q17=sQuery(id+"F12.wireOp",EDGE,"E35.top");
            var Q18;
            Q18=sQuery(id+"F12.wireOp",EDGE,"E35.left");
            var Q19;
            Q19=sQuery(id+"F12.wireOp",EDGE,"E35.right");
            var Q20;
            Q20=sQuery(id+"F12.wireOp",EDGE,"E36.1.0.0");
            var Q21;
            Q21=sQuery(id+"F12.wireOp",EDGE,"E36.1.0.1");
            var Q22;
            Q22=sQuery(id+"F12.wireOp",EDGE,"E36.1.0.2");
            var Q23;
            Q23=sQuery(id+"F12.wireOp",EDGE,"E36.1.0.3");
            var Q24;
            Q24=sQuery(id+"F12.wireOp",EDGE,"E36.2.0.0");
            var Q25;
            Q25=sQuery(id+"F12.wireOp",EDGE,"E36.2.0.1");
            var Q26;
            Q26=sQuery(id+"F12.wireOp",EDGE,"E36.2.0.2");
            var Q27;
            Q27=sQuery(id+"F12.wireOp",EDGE,"E36.2.0.3");
            var Q28;
            Q28=sQuery(id+"F12.wireOp",EDGE,"E36.3.0.0");
            var Q29;
            Q29=sQuery(id+"F12.wireOp",EDGE,"E36.3.0.1");
            var Q30;
            Q30=sQuery(id+"F12.wireOp",EDGE,"E36.3.0.2");
            var Q31;
            Q31=sQuery(id+"F12.wireOp",EDGE,"E36.3.0.3");
            var Q32;
            Q32=sQuery(id+"F12.wireOp",EDGE,"E36.4.0.0");
            var Q33;
            Q33=sQuery(id+"F12.wireOp",EDGE,"E36.4.0.1");
            var Q34;
            Q34=sQuery(id+"F12.wireOp",EDGE,"E36.4.0.2");
            var Q35;
            Q35=sQuery(id+"F12.wireOp",EDGE,"E36.4.0.3");
            var Q36;
            Q36=sQuery(id+"F12.wireOp",EDGE,"E36.5.0.0");
            var Q37;
            Q37=sQuery(id+"F12.wireOp",EDGE,"E36.5.0.1");
            var Q38;
            Q38=sQuery(id+"F12.wireOp",EDGE,"E36.5.0.2");
            var Q39;
            Q39=sQuery(id+"F12.wireOp",EDGE,"E36.5.0.3");
            var Q40;
            Q40=sQuery(id+"F12.wireOp",EDGE,"E36.6.0.0");
            var Q41;
            Q41=sQuery(id+"F12.wireOp",EDGE,"E36.6.0.1");
            var Q42;
            Q42=sQuery(id+"F12.wireOp",EDGE,"E36.6.0.2");
            var Q43;
            Q43=sQuery(id+"F12.wireOp",EDGE,"E36.6.0.3");
            var Q44;
            Q44=sQuery(id+"F12.wireOp",EDGE,"E36.7.0.0");
            var Q45;
            Q45=sQuery(id+"F12.wireOp",EDGE,"E36.7.0.1");
            var Q46;
            Q46=sQuery(id+"F12.wireOp",EDGE,"E36.7.0.2");
            var Q47;
            Q47=sQuery(id+"F12.wireOp",EDGE,"E36.7.0.3");
            extrude(context, id + "F13", {"entities" : qUnion([Q0, Q1, Q2, Q3, Q4, Q5, Q6, Q7, Q8, Q9, Q10, Q11, Q12, Q13, Q14, Q15]), "operationType" : NewBodyOperationType.REMOVE, "surfaceEntities" : qUnion([Q16, Q17, Q18, Q19, Q20, Q21, Q22, Q23, Q24, Q25, Q26, Q27, Q28, Q29, Q30, Q31, Q32, Q33, Q34, Q35, Q36, Q37, Q38, Q39, Q40, Q41, Q42, Q43, Q44, Q45, Q46, Q47]), "oppositeDirection" : true, "depth" : 7 * mm});
        }
        {
            var Q0;
            Q0=makeQuery(id+"F0.imprint","IMPRINT",FACE,{"disambiguationData":[TD([[makeQuery(id+"F0.imprint","IMPRINT",EDGE,{"derivedFrom":sQuery(id+"F0.wireOp",EDGE,"E15.bottom")}),-1.0]])]});
            extrude(context, id + "F14", {"entities" : qUnion([Q0]), "operationType" : NewBodyOperationType.ADD, "depth" : 4 * mm});
        }
        {
            var Q0;
            Q0=makeQuery(id+"F14.opExtrude","CAP_FACE",FACE,{"disambiguationData":[OSD([sQuery(id+"F0.wireOp",EDGE,"E15.bottom"),sQuery(id+"F0.wireOp",EDGE,"E15.top"),sQuery(id+"F0.wireOp",EDGE,"E15.left"),sQuery(id+"F0.wireOp",EDGE,"E15.right")])],"isStart":false});
            var sketch = newSketch(context, id + "F15", { "sketchPlane" : qUnion([Q0])});
            skLineSegment(sketch, "E37.bottom", {"start": v(-10.41, 2.12) * mm, "end": v(25.59, 2.12) * mm});
            skLineSegment(sketch, "E37.top", {"start": v(-10.41, -2.2) * mm, "end": v(25.59, -2.2) * mm});
            skLineSegment(sketch, "E37.left", {"start": v(-10.41, 2.12) * mm, "end": v(-10.41, -2.2) * mm});
            skLineSegment(sketch, "E37.right", {"start": v(25.59, 2.12) * mm, "end": v(25.59, -2.2) * mm});
            skSolve(sketch);
        }
        {
            var Q0;
            Q0=makeQuery(id+"F15.imprint","IMPRINT",FACE,{"disambiguationData":[TD([[makeQuery(id+"F15.imprint","IMPRINT",EDGE,{"derivedFrom":sQuery(id+"F15.wireOp",EDGE,"E37.bottom")}),-1.0]])]});
            extrude(context, id + "F16", {"entities" : qUnion([Q0]), "operationType" : NewBodyOperationType.ADD, "depth" : 1 * mm});
        }
        {
            var Q0;
            Q0=makeQuery(id+"F0.imprint","IMPRINT",FACE,{"disambiguationData":[TD([[makeQuery(id+"F0.imprint","IMPRINT",EDGE,{"derivedFrom":sQuery(id+"F0.wireOp",EDGE,"E17")}),1.0]])]});
            var Q1;
            Q1=makeQuery(id+"F0.imprint","IMPRINT",FACE,{"disambiguationData":[TD([[makeQuery(id+"F0.imprint","IMPRINT",EDGE,{"derivedFrom":sQuery(id+"F0.wireOp",EDGE,"E16")}),1.0]])]});
            extrude(context, id + "F17", {"entities" : qUnion([Q0, Q1]), "depth" : 7 * mm});
        }
        {
            var Q0;
            Q0=makeQuery(id+"F0.imprint","IMPRINT",FACE,{"disambiguationData":[TD([[makeQuery(id+"F0.imprint","IMPRINT",EDGE,{"derivedFrom":sQuery(id+"F0.wireOp",EDGE,"E19.bottom")}),-1.0]])]});
            extrude(context, id + "F18", {"entities" : qUnion([Q0]), "depth" : 5 * mm});
        }
        {
            var Q0;
            Q0=makeQuery(id+"F18.opExtrude","CAP_FACE",FACE,{"disambiguationData":[OSD([sQuery(id+"F0.wireOp",EDGE,"E19.bottom"),sQuery(id+"F0.wireOp",EDGE,"E19.top"),sQuery(id+"F0.wireOp",EDGE,"E19.left"),sQuery(id+"F0.wireOp",EDGE,"E19.right")])],"isStart":false});
            var sketch = newSketch(context, id + "F19", { "sketchPlane" : qUnion([Q0])});
            skLineSegment(sketch, "E38.bottom", {"start": v(-36.21, 18.32) * mm, "end": v(-34.21, 18.32) * mm});
            skLineSegment(sketch, "E38.top", {"start": v(-36.21, 13.32) * mm, "end": v(-34.21, 13.32) * mm});
            skLineSegment(sketch, "E38.left", {"start": v(-36.21, 18.32) * mm, "end": v(-36.21, 13.32) * mm});
            skLineSegment(sketch, "E38.right", {"start": v(-34.21, 18.32) * mm, "end": v(-34.21, 13.32) * mm});
            skSolve(sketch);
        }
        {
            var Q0;
            Q0=makeQuery(id+"F19.imprint","IMPRINT",FACE,{"disambiguationData":[TD([[makeQuery(id+"F19.imprint","IMPRINT",EDGE,{"derivedFrom":sQuery(id+"F19.wireOp",EDGE,"E38.bottom")}),-1.0]])]});
            extrude(context, id + "F20", {"entities" : qUnion([Q0]), "operationType" : NewBodyOperationType.REMOVE, "oppositeDirection" : true, "depth" : 1 * mm});
        }
        {
            var Q0;
            Q0=makeQuery(id+"F20.boolean.opBoolean","COPY",FACE,{"derivedFrom":makeQuery(id+"F20.opExtrude","CAP_FACE",FACE,{"disambiguationData":[OSD([sQuery(id+"F19.wireOp",EDGE,"E38.bottom"),sQuery(id+"F19.wireOp",EDGE,"E38.top"),sQuery(id+"F19.wireOp",EDGE,"E38.left"),sQuery(id+"F19.wireOp",EDGE,"E38.right")])],"isStart":false})});
            var sketch = newSketch(context, id + "F21", { "sketchPlane" : qUnion([Q0])});
            skLineSegment(sketch, "E39.bottom", {"start": v(-36.21, 15.82) * mm, "end": v(-34.21, 15.82) * mm});
            skLineSegment(sketch, "E39.top", {"start": v(-36.21, 13.32) * mm, "end": v(-34.21, 13.32) * mm});
            skLineSegment(sketch, "E39.left", {"start": v(-36.21, 15.82) * mm, "end": v(-36.21, 13.32) * mm});
            skLineSegment(sketch, "E39.right", {"start": v(-34.21, 15.82) * mm, "end": v(-34.21, 13.32) * mm});
            skSolve(sketch);
        }
        {
            var Q0;
            Q0=makeQuery(id+"F21.imprint","IMPRINT",FACE,{"disambiguationData":[TD([[makeQuery(id+"F21.imprint","IMPRINT",EDGE,{"derivedFrom":sQuery(id+"F21.wireOp",EDGE,"E39.bottom")}),-1.0]])]});
            extrude(context, id + "F22", {"entities" : qUnion([Q0]), "operationType" : NewBodyOperationType.ADD, "depth" : 2 * mm});
        }
        {
            var Q0;
            Q0=makeQuery(id+"F0.imprint","IMPRINT",FACE,{"disambiguationData":[TD([[makeQuery(id+"F0.imprint","IMPRINT",EDGE,{"derivedFrom":sQuery(id+"F0.wireOp",EDGE,"E20.bottom")}),-1.0]])]});
            extrude(context, id + "F23", {"entities" : qUnion([Q0]), "depth" : 3 * mm});
        }
        {
            var Q0;
            Q0=makeQuery(id+"F23.opExtrude","CAP_FACE",FACE,{"disambiguationData":[OSD([sQuery(id+"F0.wireOp",EDGE,"E20.bottom"),sQuery(id+"F0.wireOp",EDGE,"E20.top"),sQuery(id+"F0.wireOp",EDGE,"E20.left"),sQuery(id+"F0.wireOp",EDGE,"E20.right")])],"isStart":false});
            var sketch = newSketch(context, id + "F24", { "sketchPlane" : qUnion([Q0])});
            skCircle(sketch, "E40", {"center": v(18.1, 8.97) * mm, "radius": 2 * mm});
            skLineSegment(sketch, "E41", {"start": v(18.09, 11.45) * mm, "end": v(18.09, 6.45) * mm, "construction": true});
            skSolve(sketch);
        }
        {
            var Q0;
            Q0=makeQuery(id+"F24.imprint","IMPRINT",FACE,{"disambiguationData":[TD([[makeQuery(id+"F24.imprint","IMPRINT",EDGE,{"derivedFrom":sQuery(id+"F24.wireOp",EDGE,"E40")}),1.0]])]});
            extrude(context, id + "F25", {"entities" : qUnion([Q0]), "operationType" : NewBodyOperationType.ADD, "depth" : 0.5 * mm});
        }
        {
            var Q0;
            Q0=makeQuery(id+"F23.opExtrude","CAP_FACE",FACE,{"disambiguationData":[OSD([sQuery(id+"F0.wireOp",EDGE,"E20.bottom"),sQuery(id+"F0.wireOp",EDGE,"E20.top"),sQuery(id+"F0.wireOp",EDGE,"E20.left"),sQuery(id+"F0.wireOp",EDGE,"E20.right")])],"isStart":false});
            var sketch = newSketch(context, id + "F26", { "sketchPlane" : qUnion([Q0])});
            skCircle(sketch, "E42", {"center": v(16.17, 10.87) * mm, "radius": 0.5 * mm});
            skCircle(sketch, "E43", {"center": v(19.97, 10.87) * mm, "radius": 0.5 * mm});
            skCircle(sketch, "E44", {"center": v(19.99, 7.02) * mm, "radius": 0.5 * mm});
            skCircle(sketch, "E45", {"center": v(16.19, 7.04) * mm, "radius": 0.5 * mm});
            skSolve(sketch);
        }
        {
            var Q0;
            Q0=makeQuery(id+"F26.imprint","IMPRINT",FACE,{"disambiguationData":[TD([[makeQuery(id+"F26.imprint","IMPRINT",EDGE,{"derivedFrom":sQuery(id+"F26.wireOp",EDGE,"E42")}),1.0]])]});
            var Q1;
            Q1=makeQuery(id+"F26.imprint","IMPRINT",FACE,{"disambiguationData":[TD([[makeQuery(id+"F26.imprint","IMPRINT",EDGE,{"derivedFrom":sQuery(id+"F26.wireOp",EDGE,"E45")}),1.0]])]});
            var Q2;
            Q2=makeQuery(id+"F26.imprint","IMPRINT",FACE,{"disambiguationData":[TD([[makeQuery(id+"F26.imprint","IMPRINT",EDGE,{"derivedFrom":sQuery(id+"F26.wireOp",EDGE,"E44")}),1.0]])]});
            var Q3;
            Q3=makeQuery(id+"F26.imprint","IMPRINT",FACE,{"disambiguationData":[TD([[makeQuery(id+"F26.imprint","IMPRINT",EDGE,{"derivedFrom":sQuery(id+"F26.wireOp",EDGE,"E43")}),1.0]])]});
            extrude(context, id + "F27", {"entities" : qUnion([Q0, Q1, Q2, Q3]), "operationType" : NewBodyOperationType.ADD, "depth" : 0.12 * mm});
        }
        {
            var Q0;
            {var subQ0=sQuery(id+"F0.wireOp",EDGE,"E0.left");Q0=makeQuery(id+"F1.opExtrude","SWEPT_FACE",FACE,{"disambiguationData":[OSD([subQ0]),TDD([makeQuery(id+"F0.imprint","IMPRINT",EDGE,{"disambiguationData":[TD([[makeQuery(id+"F0.imprint","INTERSECT",VERTEX,{"derivedFrom":[sQuery(id+"F0.wireOp",EDGE,"E0.top"),subQ0]}),1.0]])],"derivedFrom":subQ0})])]});}
            var sketch = newSketch(context, id + "F28", { "sketchPlane" : qUnion([Q0])});
            skLineSegment(sketch, "E46.bottom", {"start": v(2.55, 9.97) * mm, "end": v(11.55, 9.97) * mm});
            skLineSegment(sketch, "E46.top", {"start": v(2.55, -0.03) * mm, "end": v(11.55, -0.03) * mm});
            skLineSegment(sketch, "E46.left", {"start": v(2.55, 9.97) * mm, "end": v(2.55, -0.03) * mm});
            skLineSegment(sketch, "E46.right", {"start": v(11.55, 9.97) * mm, "end": v(11.55, -0.03) * mm});
            skSolve(sketch);
        }
        {
            var Q0;
            Q0=qSketchRegion(id+"F28",true);
            extrude(context, id + "F29", {"entities" : qUnion([Q0]), "operationType" : NewBodyOperationType.ADD, "depth" : 3 * mm});
        }
        {
            var Q0;
            Q0=makeQuery(id+"F29.opExtrude","CAP_FACE",FACE,{"disambiguationData":[OSD([sQuery(id+"F28.wireOp",EDGE,"E46.bottom"),sQuery(id+"F28.wireOp",EDGE,"E46.top"),sQuery(id+"F28.wireOp",EDGE,"E46.left"),sQuery(id+"F28.wireOp",EDGE,"E46.right")])],"isStart":true});
            var sketch = newSketch(context, id + "F30", { "sketchPlane" : qUnion([Q0])});
            skArc(sketch, "E47", {"start": v(-7.05, 9.97) * mm, "mid": v(-9.89, 9) * mm, "end": v(-11.55, 6.5) * mm});
            skArc(sketch, "E48", {"start": v(-2.55, 6.5) * mm, "mid": v(-4.21, 9) * mm, "end": v(-7.05, 9.97) * mm});
            skLineSegment(sketch, "E49", {"start": v(-11.55, 6.5) * mm, "end": v(-11.55, 0) * mm});
            skLineSegment(sketch, "E50", {"start": v(-11.55, 0) * mm, "end": v(-2.55, 0) * mm});
            skLineSegment(sketch, "E51", {"start": v(-2.55, 0) * mm, "end": v(-2.55, 6.5) * mm});
            skSolve(sketch);
        }
        {
            var Q0;
            Q0=qSketchRegion(id+"F30",true);
            extrude(context, id + "F31", {"entities" : qUnion([Q0]), "operationType" : NewBodyOperationType.ADD, "depth" : 10 * mm});
        }
        {
            var Q0;
            Q0=makeQuery(id+"F29.opExtrude","CAP_FACE",FACE,{"disambiguationData":[OSD([sQuery(id+"F28.wireOp",EDGE,"E46.bottom"),sQuery(id+"F28.wireOp",EDGE,"E46.top"),sQuery(id+"F28.wireOp",EDGE,"E46.left"),sQuery(id+"F28.wireOp",EDGE,"E46.right")])],"isStart":false});
            var sketch = newSketch(context, id + "F32", { "sketchPlane" : qUnion([Q0])});
            skCircle(sketch, "E52", {"center": v(7.05, 5.5) * mm, "radius": 3.5 * mm});
            skSolve(sketch);
        }
        {
            var Q0;
            Q0=makeQuery(id+"F32.imprint","IMPRINT",FACE,{"disambiguationData":[TD([[makeQuery(id+"F32.imprint","IMPRINT",EDGE,{"derivedFrom":sQuery(id+"F32.wireOp",EDGE,"E52")}),1.0]])]});
            extrude(context, id + "F33", {"entities" : qUnion([Q0]), "operationType" : NewBodyOperationType.REMOVE, "oppositeDirection" : true, "depth" : 10 * mm});
        }
        {
            var Q0;
            Q0=makeQuery(id+"F33.boolean.opBoolean","COPY",FACE,{"derivedFrom":makeQuery(id+"F33.opExtrude","CAP_FACE",FACE,{"disambiguationData":[OSD([sQuery(id+"F32.wireOp",EDGE,"E52")])],"isStart":false})});
            var sketch = newSketch(context, id + "F34", { "sketchPlane" : qUnion([Q0])});
            skCircle(sketch, "E53", {"center": v(7.05, 5.5) * mm, "radius": 0.5 * mm});
            skSolve(sketch);
        }
        {
            var Q0;
            Q0=qSketchRegion(id+"F34",true);
            extrude(context, id + "F35", {"entities" : qUnion([Q0]), "operationType" : NewBodyOperationType.ADD, "depth" : 8 * mm});
        }
    });
